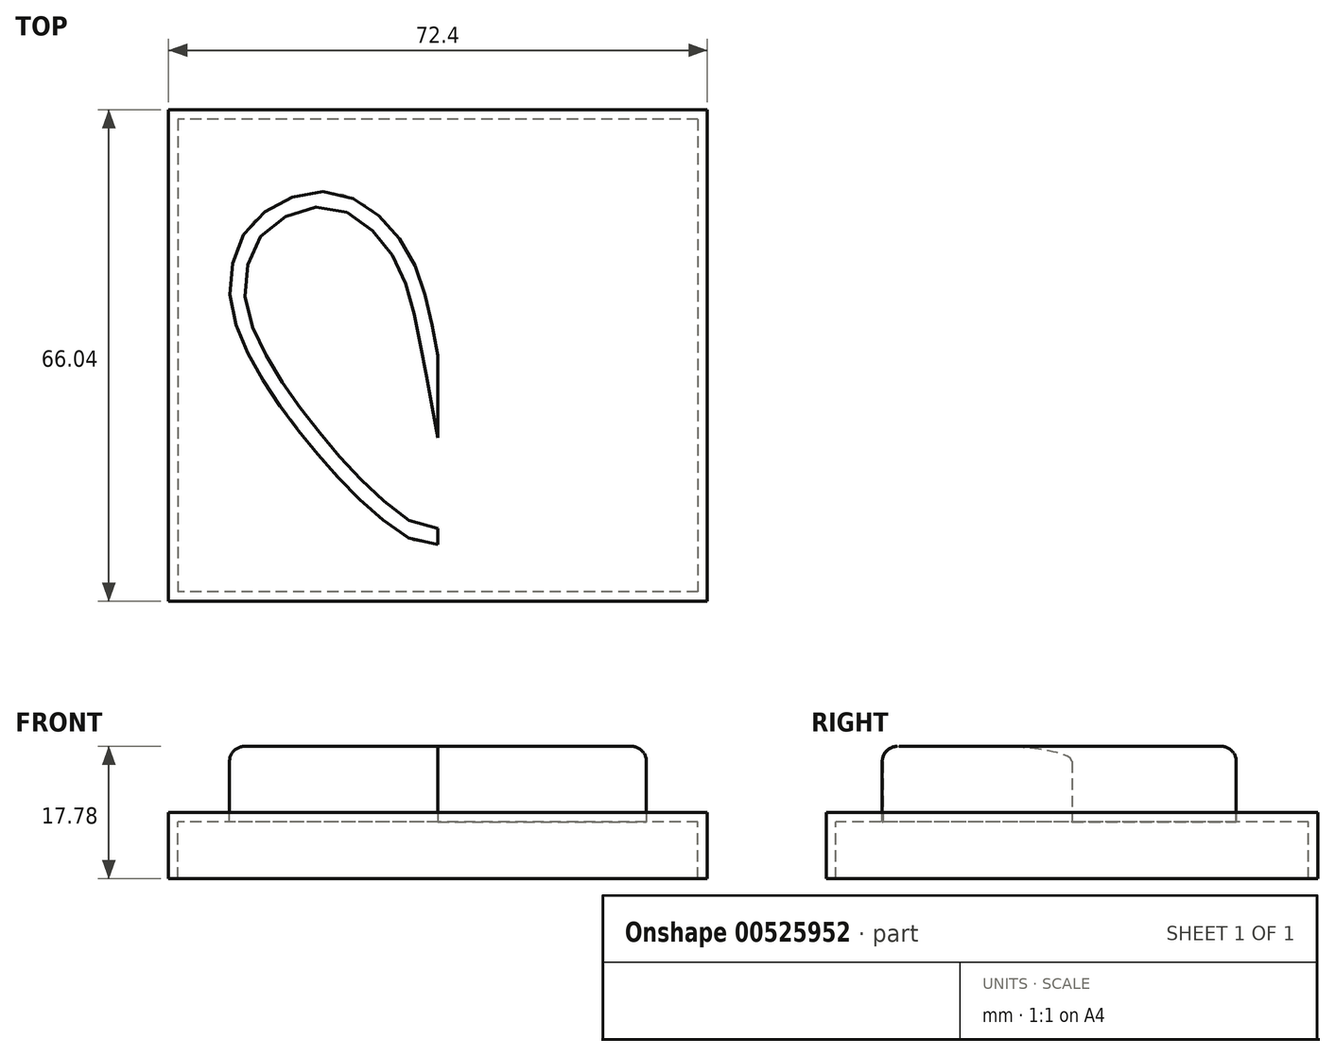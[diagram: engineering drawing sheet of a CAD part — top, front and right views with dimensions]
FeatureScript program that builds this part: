
annotation { "Feature Type Name" : "Feature", "Feature Type Description" : "" }
export const myFeature = defineFeature(function(context is Context, id is Id, definition is map)
    precondition{}
    {
        {
            var Q0;
            Q0=qCreatedBy(makeId("Top.planeOp"),FACE);
            var sketch = newSketch(context, id + "F0", { "sketchPlane" : qUnion([Q0])});
            skFitSpline(sketch, "E0", {"points": [v(0, 0) * mm, v(-4.77, 15.15) * mm, v(-14.25, 21.95) * mm, v(-24.2, 18.54) * mm, v(-27.43, 13) * mm, v(-25.4, 0) * mm, v(0, -25.4) * mm, v(0, 0) * mm]});
            skFitSpline(sketch, "E1.MirrorC", {"points": [v(0, 0) * mm, v(4.77, 15.15) * mm, v(14.25, 21.95) * mm, v(24.2, 18.54) * mm, v(27.43, 13) * mm, v(25.4, 0) * mm, v(0, -25.4) * mm, v(0, 0) * mm]});
            skSolve(sketch);
        }
        {
            var Q0;
            {var subQ0=sQuery(id+"F0.wireOp",EDGE,"E1.MirrorC");var subQ1=sQuery(id+"F0.wireOp",EDGE,"E0");var subQ2=makeQuery(id+"F0.imprint","INTERSECT",VERTEX,{"disambiguationData":[OD(0.0)],"derivedFrom":[subQ1,subQ0]});Q0=makeQuery(id+"F0.imprint","IMPRINT",FACE,{"disambiguationData":[TD([[makeQuery(id+"F0.imprint","IMPRINT",EDGE,{"disambiguationData":[TD([[subQ2,1.0]])],"derivedFrom":subQ1}),1.0]])]});}
            var Q1;
            {var subQ0=sQuery(id+"F0.wireOp",EDGE,"E1.MirrorC");var subQ1=sQuery(id+"F0.wireOp",EDGE,"E0");var subQ2=makeQuery(id+"F0.imprint","INTERSECT",VERTEX,{"disambiguationData":[OD(0.0)],"derivedFrom":[subQ1,subQ0]});Q1=makeQuery(id+"F0.imprint","IMPRINT",FACE,{"disambiguationData":[TD([[makeQuery(id+"F0.imprint","IMPRINT",EDGE,{"disambiguationData":[TD([[subQ2,-1.0]])],"derivedFrom":subQ1}),-1.0]])]});}
            var Q2;
            {var subQ0=sQuery(id+"F0.wireOp",EDGE,"E1.MirrorC");var subQ1=sQuery(id+"F0.wireOp",EDGE,"E0");var subQ2=makeQuery(id+"F0.imprint","INTERSECT",VERTEX,{"disambiguationData":[OD(0.0)],"derivedFrom":[subQ1,subQ0]});Q2=makeQuery(id+"F0.imprint","IMPRINT",FACE,{"disambiguationData":[TD([[makeQuery(id+"F0.imprint","IMPRINT",EDGE,{"disambiguationData":[TD([[subQ2,-1.0]])],"derivedFrom":subQ1}),1.0]])]});}
            extrude(context, id + "F1", {"entities" : qUnion([Q0, Q1, Q2]), "depth" : 10.16 * mm, "offsetDistance" : 25.4 * mm});
        }
        {
            var Q0;
            Q0=qCreatedBy(makeId("Top.planeOp"),FACE);
            var sketch = newSketch(context, id + "F2", { "sketchPlane" : qUnion([Q0])});
            skLineSegment(sketch, "E2.bottom", {"start": v(34.92, 31.75) * mm, "end": v(-34.93, 31.75) * mm});
            skLineSegment(sketch, "E2.top", {"start": v(34.93, -31.75) * mm, "end": v(-34.92, -31.75) * mm});
            skLineSegment(sketch, "E2.left", {"start": v(34.92, 31.75) * mm, "end": v(34.93, -31.75) * mm});
            skLineSegment(sketch, "E2.right", {"start": v(-34.93, 31.75) * mm, "end": v(-34.92, -31.75) * mm});
            skSolve(sketch);
        }
        {
            var Q0;
            Q0 = qSketchRegion(id + "F2", true);
            extrude(context, id + "F3", {"entities" : qUnion([Q0]), "oppositeDirection" : true, "depth" : 7.62 * mm, "offsetDistance" : 25.4 * mm});
        }
        {
            var Q0;
            Q0=makeQuery(id+"F1.opExtrude","CAP_EDGE",EDGE,{"disambiguationData":[OSD([sQuery(id+"F0.wireOp",EDGE,"E0")])],"isStart":false});
            var Q1;
            Q1=makeQuery(id+"F1.opExtrude","CAP_EDGE",EDGE,{"disambiguationData":[OSD([sQuery(id+"F0.wireOp",EDGE,"E1.MirrorC")])],"isStart":false});
            fillet(context, id + "F4", {"entities" : qUnion([Q0, Q1]), "radius" : 2.03 * mm, "tangentPropagation" : true, "allowEdgeOverflow" : false});
        }
        {
            var Q0;
            Q0=makeQuery(id+"F3.opExtrude","CAP_FACE",FACE,{"disambiguationData":[OSD([sQuery(id+"F2.wireOp",EDGE,"E2.bottom"),sQuery(id+"F2.wireOp",EDGE,"E2.top"),sQuery(id+"F2.wireOp",EDGE,"E2.left"),sQuery(id+"F2.wireOp",EDGE,"E2.right")])],"isStart":false});
            var Q1;
            Q1=makeQuery(id+"F3.opExtrude","SWEPT_BODY",BODY,{"disambiguationData":[OSD([sQuery(id+"F2.wireOp",EDGE,"E2.bottom"),sQuery(id+"F2.wireOp",EDGE,"E2.top"),sQuery(id+"F2.wireOp",EDGE,"E2.left"),sQuery(id+"F2.wireOp",EDGE,"E2.right")])]});
            shell(context, id + "F5", {"entities" : qUnion([Q0]), "parts" : qUnion([Q1]), "thickness" : 1.27 * mm, "oppositeDirection" : true});
        }
    });
